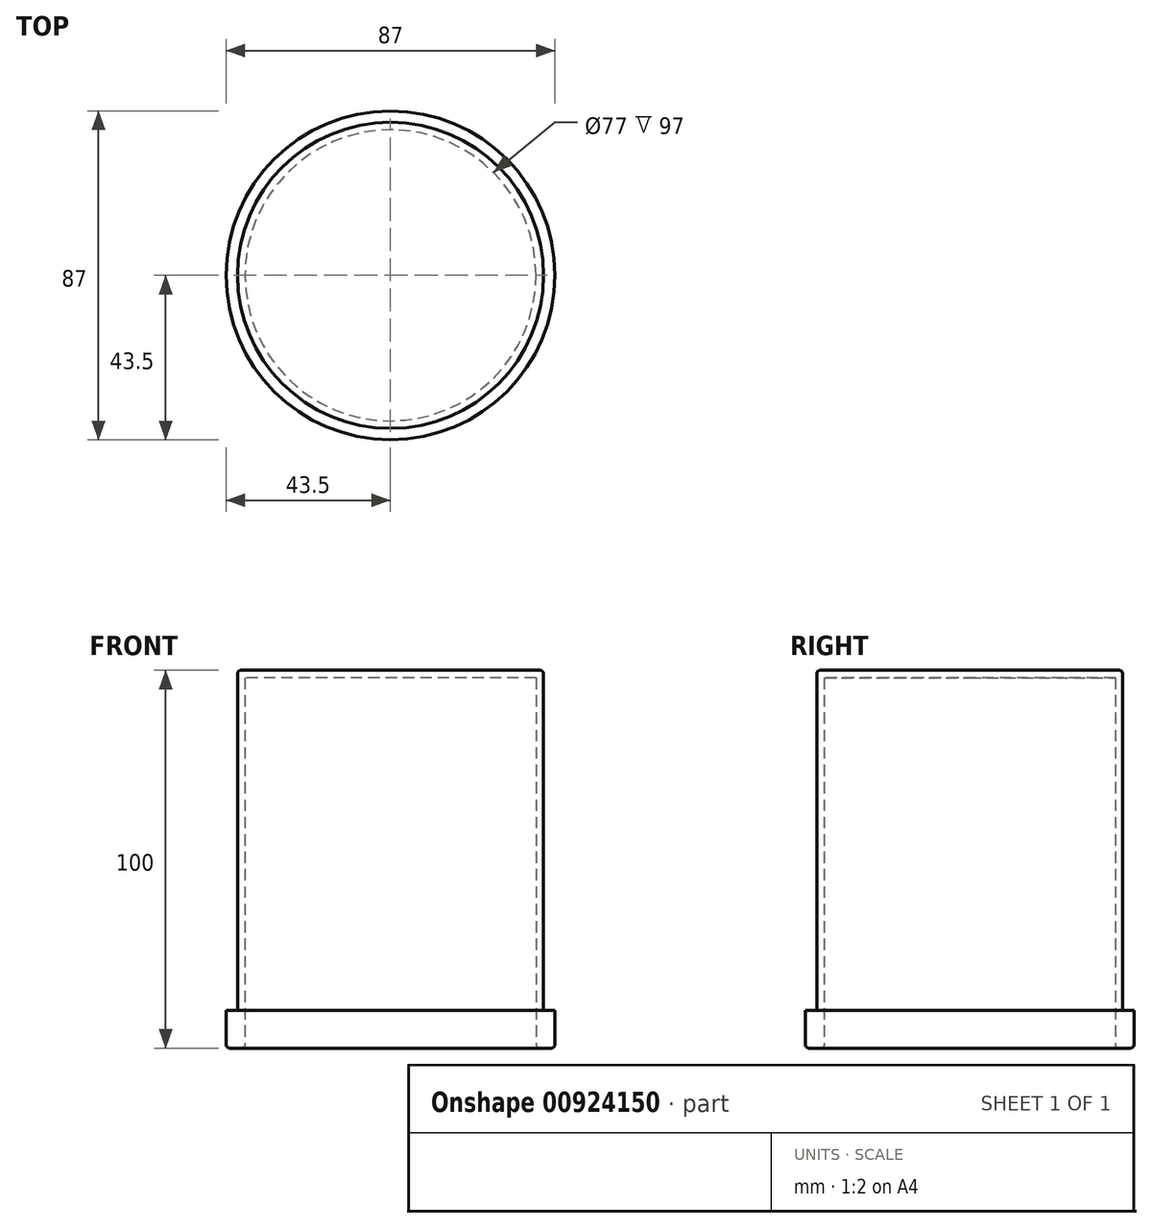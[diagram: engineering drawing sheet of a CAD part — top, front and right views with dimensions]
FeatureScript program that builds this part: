
annotation { "Feature Type Name" : "Feature", "Feature Type Description" : "" }
export const myFeature = defineFeature(function(context is Context, id is Id, definition is map)
    precondition{}
    {
        {
            var Q0;
            Q0=qCreatedBy(makeId("Top.planeOp"),FACE);
            var sketch = newSketch(context, id + "F0", { "sketchPlane" : qUnion([Q0])});
            skCircle(sketch, "E0", {"center": v(0, 0) * mm, "radius": 43.5 * mm});
            skCircle(sketch, "E1", {"center": v(0, 0) * mm, "radius": 38.5 * mm});
            skSolve(sketch);
        }
        {
            var Q0;
            Q0=makeQuery(id+"F0.imprint","IMPRINT",FACE,{"disambiguationData":[TD([[makeQuery(id+"F0.imprint","IMPRINT",EDGE,{"derivedFrom":sQuery(id+"F0.wireOp",EDGE,"E0")}),1.0]])]});
            extrude(context, id + "F1", {"entities" : qUnion([Q0]), "depth" : 10 * mm, "offsetDistance" : 25 * mm});
        }
        {
            var Q0;
            Q0=makeQuery(id+"F1.opExtrude","CAP_FACE",FACE,{"disambiguationData":[OSD([sQuery(id+"F0.wireOp",EDGE,"E0"),sQuery(id+"F0.wireOp",EDGE,"E1")])],"isStart":false});
            var sketch = newSketch(context, id + "F2", { "sketchPlane" : qUnion([Q0])});
            skCircle(sketch, "E2", {"center": v(0, 0) * mm, "radius": 38.5 * mm});
            skCircle(sketch, "E3", {"center": v(0, 0) * mm, "radius": 40.5 * mm});
            skSolve(sketch);
        }
        {
            var Q0;
            Q0 = qSketchRegion(id + "F2", true);
            extrude(context, id + "F3", {"entities" : qUnion([Q0]), "operationType" : NewBodyOperationType.ADD, "depth" : 90 * mm, "offsetDistance" : 25 * mm});
        }
        {
            var Q0;
            Q0=makeQuery(id+"F3.opExtrude","CAP_FACE",FACE,{"disambiguationData":[OSD([sQuery(id+"F2.wireOp",EDGE,"E2"),sQuery(id+"F2.wireOp",EDGE,"E3")])],"isStart":false});
            var sketch = newSketch(context, id + "F4", { "sketchPlane" : qUnion([Q0])});
            skCircle(sketch, "E4", {"center": v(0, 0) * mm, "radius": 38.5 * mm});
            skSolve(sketch);
        }
        {
            var Q0;
            Q0 = qSketchRegion(id + "F4", true);
            extrude(context, id + "F5", {"entities" : qUnion([Q0]), "operationType" : NewBodyOperationType.ADD, "oppositeDirection" : true, "depth" : 2 * mm, "offsetDistance" : 25 * mm});
        }
        {
            var Q0;
            Q0=makeQuery(id+"F1.opExtrude","CAP_EDGE",EDGE,{"disambiguationData":[OSD([sQuery(id+"F0.wireOp",EDGE,"E0")])],"isStart":true});
            var Q1;
            Q1=makeQuery(id+"F1.opExtrude","CAP_EDGE",EDGE,{"disambiguationData":[OSD([sQuery(id+"F0.wireOp",EDGE,"E1")])],"isStart":true});
            var Q2;
            Q2=makeQuery(id+"F3.opExtrude","CAP_EDGE",EDGE,{"disambiguationData":[OSD([sQuery(id+"F2.wireOp",EDGE,"E3")])],"isStart":false});
            var Q3;
            Q3=makeQuery(id+"F5.opExtrude","CAP_EDGE",EDGE,{"disambiguationData":[OSD([sQuery(id+"F4.wireOp",EDGE,"E4")])],"isStart":false});
            fillet(context, id + "F6", {"entities" : qUnion([Q0, Q1, Q2, Q3]), "radius" : 1 * mm, "tangentPropagation" : true, "allowEdgeOverflow" : false});
        }
    });
